# Revit family: LPB
name_source: partatom
category: Mechanical Equipment
units: mm (PartAtom-declared; Revit-internal decimal feet)

## family parameters
Always vertical = Yes
Cut with Voids When Loaded = No
Part Type = Normal
Room Calculation Point = No
Round Connector Dimension = Use Diameter
Shared = No
Work Plane-Based = No

## types (18) — shared parameters
0 = 0' - 0"
1" = 0' - 1"
1.5 = 0' - 1 1/2"
2" = 0' - 2"
2' = 2' - 0"
3" = 0' - 3"
4" = 0' - 4"
Manufacturer = Loren Cook Company
Model = LPB
ONE EIGTH = 0' - 0 1/8"
Type Comments = Low Profile Centrifugal Exhaust Ventilator Roof Mounted/Belt Drive
URL = www.lorencook.com

## per-type parameters (varying)
| type | (F-B)/2 | -(D+1") | A | A/2 | B | B/2 | C | C+G | C/2 | D | E | F | F/2 | G | G-.125" | H | I | J | RO | RO/2 | T_SQ | T_SQ/2 |
| 100_LPB | 0' - 11 5/32" | -0' - 7 11/16" | 1' - 10 1/16" | 0' - 11 1/32" | 2' - 5 7/8" | 1' - 2 15/16" | 1' - 1 7/8" | 1' - 3 7/8" | 0' - 6 15/16" | 0' - 6 11/16" | 0' - 6 25/32" | 4' - 4 3/16" | 2' - 2 3/32" | 0' - 2" | 0' - 1 7/8" | 0' - 1 1/32" | 0' - 8 19/32" | 0' - 1 9/32" | 1' - 3 1/2" | 0' - 7 3/4" | 1' - 8" | 0' - 10" |
| 120_LPB | 1' - 1 7/32" | -0' - 9" | 2' - 1 11/16" | 1' - 0 27/32" | 2' - 8 3/8" | 1' - 4 3/16" | 1' - 3 3/8" | 1' - 5 3/8" | 0' - 7 11/16" | 0' - 8" | 0' - 8 5/32" | 4' - 10 13/16" | 2' - 5 13/32" | 0' - 2" | 0' - 1 7/8" | 0' - 0 27/32" | 0' - 7 29/32" | 0' - 0 15/32" | 1' - 7 1/2" | 0' - 9 3/4" | 2' - 0" | 1' - 0" |
| 135_LPB | 1' - 2 13/16" | -0' - 10" | 2' - 4 7/16" | 1' - 2 7/32" | 2' - 10 1/2" | 1' - 5 1/4" | 1' - 4 3/8" | 1' - 6 3/8" | 0' - 8 3/16" | 0' - 9" | 0' - 9 3/16" | 5' - 4 1/8" | 2' - 8 1/16" | 0' - 2" | 0' - 1 7/8" | 0' - 2 7/32" | 0' - 8 15/16" | 0' - 1 9/16" | 1' - 7 1/2" | 0' - 9 3/4" | 2' - 0" | 1' - 0" |
| 150_LPB | 1' - 4 11/32" | -0' - 11" | 2' - 7 1/8" | 1' - 3 9/16" | 3' - 0 11/16" | 1' - 6 11/32" | 1' - 5 3/8" | 1' - 7 3/8" | 0' - 8 11/16" | 0' - 10" | 0' - 10 7/32" | 5' - 9 3/8" | 2' - 10 11/16" | 0' - 2" | 0' - 1 7/8" | 0' - 3 9/16" | 0' - 9 15/16" | 0' - 2 3/4" | 1' - 7 1/2" | 0' - 9 3/4" | 2' - 0" | 1' - 0" |
| 165_LPB | 1' - 5 27/32" | -1' - 0" | 2' - 9 13/16" | 1' - 4 29/32" | 3' - 3" | 1' - 7 1/2" | 1' - 6 3/8" | 1' - 8 3/8" | 0' - 9 3/16" | 0' - 11" | 0' - 11 7/32" | 6' - 2 11/16" | 3' - 1 11/32" | 0' - 2" | 0' - 1 7/8" | 0' - 4 29/32" | 0' - 10 15/16" | 0' - 4 1/16" | 1' - 7 1/2" | 0' - 9 3/4" | 2' - 0" | 1' - 0" |
| 180_LPB | 1' - 7 3/8" | -1' - 1" | 3' - 0 1/2" | 1' - 6 1/4" | 3' - 4 13/16" | 1' - 8 13/32" | 1' - 8 3/8" | 1' - 10 3/8" | 0' - 10 3/16" | 1' - 0" | 1' - 0 1/4" | 6' - 7 9/16" | 3' - 3 25/32" | 0' - 2" | 0' - 1 7/8" | 0' - 3 1/4" | 0' - 8 7/8" | 0' - 1 15/16" | 2' - 1 1/2" | 1' - 0 3/4" | 2' - 6" | 1' - 3" |
| 195_LPB | 1' - 8 7/8" | -1' - 2" | 3' - 3 1/4" | 1' - 7 5/8" | 4' - 1" | 2' - 0 1/2" | 1' - 9 3/8" | 1' - 11 3/8" | 0' - 10 11/16" | 1' - 1" | 1' - 1 1/4" | 7' - 6 3/4" | 3' - 9 3/8" | 0' - 2" | 0' - 1 7/8" | 0' - 4 5/8" | 1' - 4 3/16" | 0' - 2 13/16" | 2' - 1 1/2" | 1' - 0 3/4" | 2' - 6" | 1' - 3" |
| 210_LPB | 1' - 10 13/32" | -1' - 3" | 3' - 6" | 1' - 9" | 4' - 2 15/16" | 2' - 1 15/32" | 1' - 11 3/8" | 2' - 2 3/8" | 0' - 11 11/16" | 1' - 2" | 1' - 2 9/32" | 7' - 11 3/4" | 3' - 11 7/8" | 0' - 3" | 0' - 2 7/8" | 0' - 6" | 1' - 5 1/4" | 0' - 3 11/16" | 2' - 1 1/2" | 1' - 0 3/4" | 2' - 6" | 1' - 3" |
| 225_LPB | 1' - 11 15/16" | -1' - 4" | 3' - 8 5/8" | 1' - 10 5/16" | 4' - 4 11/16" | 2' - 2 11/32" | 2' - 1 1/4" | 2' - 4 1/4" | 1' - 0 5/8" | 1' - 3" | 1' - 3 5/16" | 8' - 4 9/16" | 4' - 2 9/32" | 0' - 3" | 0' - 2 7/8" | 0' - 7 5/16" | 1' - 6 5/32" | 0' - 4 17/32" | 2' - 1 1/2" | 1' - 0 3/4" | 2' - 6" | 1' - 3" |
| 245_LPB | 2' - 1 3/8" | -1' - 5" | 4' - 0 5/16" | 2' - 0 5/32" | 4' - 7 3/16" | 2' - 3 19/32" | 2' - 2 1/2" | 2' - 5 1/2" | 1' - 1 1/4" | 1' - 4" | 1' - 4 1/4" | 8' - 9 15/16" | 4' - 4 31/32" | 0' - 3" | 0' - 2 7/8" | 0' - 6 5/32" | 1' - 4 17/32" | 0' - 2 21/32" | 2' - 7 1/2" | 1' - 3 3/4" | 3' - 0" | 1' - 6" |
| 270_LPB | 2' - 4 15/32" | -1' - 6 15/16" | 4' - 4 13/16" | 2' - 2 13/32" | 4' - 10 1/4" | 2' - 5 1/8" | 2' - 4" | 2' - 7" | 1' - 2" | 1' - 5 15/16" | 1' - 5 31/32" | 9' - 7 3/16" | 4' - 9 19/32" | 0' - 3" | 0' - 2 7/8" | 0' - 8 13/32" | 1' - 6 5/32" | 0' - 4 3/32" | 2' - 7 1/2" | 1' - 3 3/4" | 3' - 0" | 1' - 6" |
| 300_LPB | 2' - 7 1/32" | -1' - 8 27/32" | 4' - 10 3/16" | 2' - 5 3/32" | 5' - 3 1/8" | 2' - 7 9/16" | 2' - 7 1/4" | 2' - 10 1/4" | 1' - 3 5/8" | 1' - 7 27/32" | 1' - 7 11/16" | 10' - 5 3/16" | 5' - 2 19/32" | 0' - 3" | 0' - 2 7/8" | 0' - 8 3/32" | 1' - 6 11/32" | 0' - 2 25/32" | 3' - 1 1/2" | 1' - 6 3/4" | 3' - 6" | 1' - 9" |
| 330_LPB | 2' - 9 3/32" | -1' - 10 3/4" | 5' - 3 5/8" | 2' - 7 13/16" | 5' - 6 11/16" | 2' - 9 11/32" | 2' - 8 1/4" | 2' - 11 1/4" | 1' - 4 1/8" | 1' - 9 3/4" | 1' - 9 13/32" | 11' - 0 7/8" | 5' - 6 7/16" | 0' - 3" | 0' - 2 7/8" | 0' - 10 13/16" | 1' - 8 9/32" | 0' - 4 13/32" | 3' - 1 1/2" | 1' - 6 3/4" | 3' - 6" | 1' - 9" |
| 365_LPB | 3' - 0 5/32" | -2' - 1" | 5' - 9 15/16" | 2' - 10 31/32" | 5' - 11 1/16" | 2' - 11 17/32" | 2' - 10 1/4" | 3' - 1 1/4" | 1' - 5 1/8" | 2' - 0" | 1' - 11 7/16" | 11' - 11 3/8" | 5' - 11 11/16" | 0' - 3" | 0' - 2 7/8" | 0' - 10 31/32" | 1' - 7 5/8" | 0' - 3 7/16" | 3' - 7 1/2" | 1' - 9 3/4" | 4' - 0" | 2' - 0" |
| 402_LPB | 3' - 3 11/32" | -2' - 3 13/32" | 6' - 4 3/4" | 3' - 2 3/8" | 6' - 3 11/16" | 3' - 1 27/32" | 3' - 0 3/8" | 3' - 3 3/8" | 1' - 6 3/16" | 2' - 2 13/32" | 2' - 1 9/16" | 12' - 10 3/8" | 6' - 5 3/16" | 0' - 3" | 0' - 2 7/8" | 1' - 2 3/8" | 1' - 10 5/32" | 0' - 5 17/32" | 3' - 7 1/2" | 1' - 9 3/4" | 4' - 0" | 2' - 0" |
| 445_LPB | 3' - 7" | -2' - 6 1/8" | 7' - 0 7/16" | 3' - 6 7/32" | 6' - 11 5/8" | 3' - 5 13/16" | 3' - 4" | 3' - 7" | 1' - 8" | 2' - 5 1/8" | 2' - 4" | 14' - 1 5/8" | 7' - 0 13/16" | 0' - 3" | 0' - 2 7/8" | 1' - 0 7/32" | 1' - 9 23/32" | 0' - 1 29/32" | 4' - 7 1/2" | 2' - 3 3/4" | 5' - 0" | 2' - 6" |
| 490_LPB | 3' - 10 27/32" | -2' - 9" | 7' - 8 9/16" | 3' - 10 9/32" | 7' - 7 1/4" | 3' - 9 5/8" | 3' - 6 1/2" | 3' - 9 1/2" | 1' - 9 1/4" | 2' - 8" | 2' - 6 9/16" | 15' - 4 15/16" | 7' - 8 15/32" | 0' - 3" | 0' - 2 7/8" | 1' - 4 9/32" | 2' - 2 13/16" | 0' - 4 7/16" | 4' - 7 1/2" | 2' - 3 3/4" | 5' - 0" | 2' - 6" |
| 540_LPB | 5' - 0 1/4" | -2' - 6 13/16" | 8' - 5 9/16" | 4' - 2 25/32" | 8' - 1 3/8" | 4' - 0 11/16" | 4' - 4 1/2" | 4' - 7 1/2" | 2' - 2 1/4" | 2' - 5 13/16" | 3' - 3 1/2" | 18' - 1 7/8" | 9' - 0 15/16" | 0' - 3" | 0' - 2 7/8" | 1' - 5 25/32" | 2' - 3 1/8" | 0' - 4 1/4" | 5' - 1 1/2" | 2' - 6 3/4" | 5' - 6" | 2' - 9" |

## geometry (parser evidence)
native form markers: Sweep x1
no freeform markers — native parametric forms only
